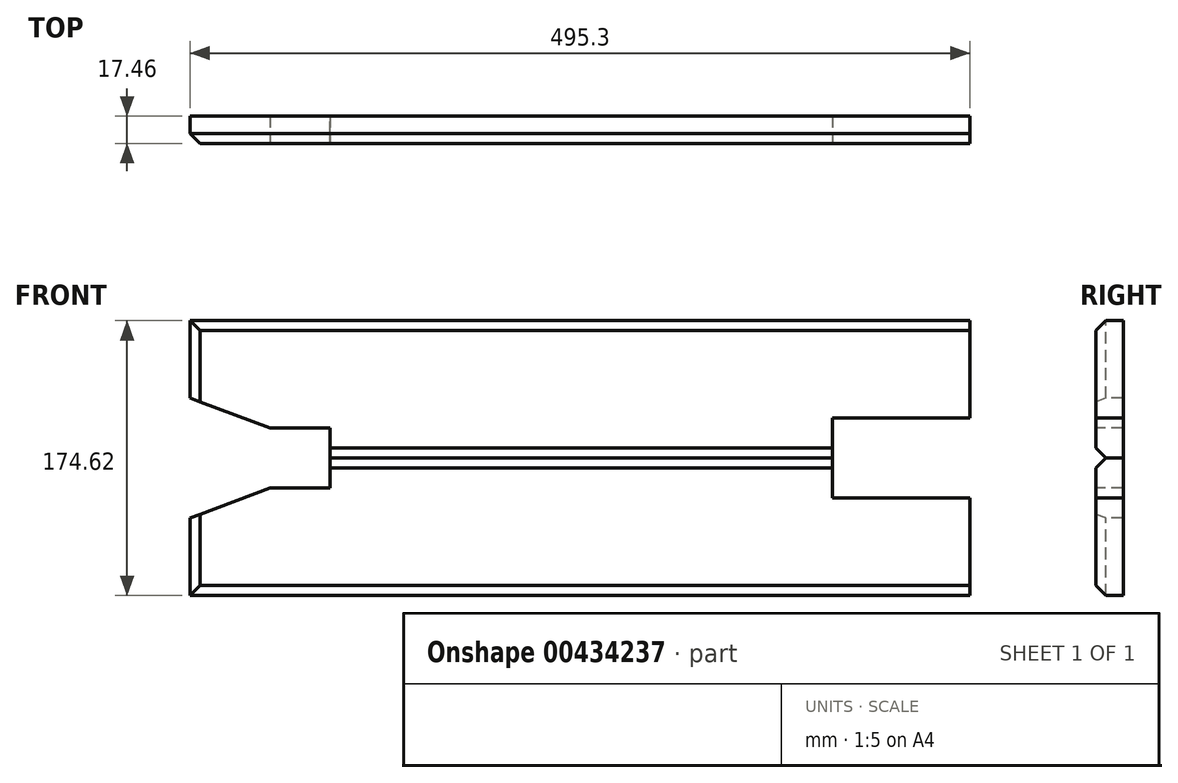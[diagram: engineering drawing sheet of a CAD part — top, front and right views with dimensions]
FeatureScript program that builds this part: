
annotation { "Feature Type Name" : "Feature", "Feature Type Description" : "" }
export const myFeature = defineFeature(function(context is Context, id is Id, definition is map)
    precondition{}
    {
        {
            var Q0;
            Q0=qCreatedBy(makeId("Front.planeOp"),FACE);
            var sketch = newSketch(context, id + "F0", { "sketchPlane" : qUnion([Q0])});
            skLineSegment(sketch, "E0.bottom", {"start": v(0, 0) * mm, "end": v(495.3, 0) * mm});
            skLineSegment(sketch, "E0.top", {"start": v(0, 87.31) * mm, "end": v(495.3, 87.31) * mm});
            skLineSegment(sketch, "E0.left", {"start": v(0, 0) * mm, "end": v(0, 87.31) * mm});
            skLineSegment(sketch, "E0.right", {"start": v(495.3, 0) * mm, "end": v(495.3, 87.31) * mm});
            skSolve(sketch);
        }
        {
            var Q0;
            Q0 = qSketchRegion(id + "F0", true);
            extrude(context, id + "F1", {"entities" : qUnion([Q0]), "depth" : 17.46 * mm});
        }
        {
            var Q0;
            Q0=makeQuery(id+"F1.opExtrude","SWEPT_FACE",FACE,{"disambiguationData":[OSD([sQuery(id+"F0.wireOp",EDGE,"E0.bottom")])]});
            var sketch = newSketch(context, id + "F2", { "sketchPlane" : qUnion([Q0])});
            skLineSegment(sketch, "E1.bottom", {"start": v(0, 0) * mm, "end": v(495.3, 0) * mm});
            skLineSegment(sketch, "E1.top", {"start": v(0, 17.46) * mm, "end": v(495.3, 17.46) * mm});
            skLineSegment(sketch, "E1.left", {"start": v(0, 0) * mm, "end": v(0, 17.46) * mm});
            skLineSegment(sketch, "E1.right", {"start": v(495.3, 0) * mm, "end": v(495.3, 17.46) * mm});
            skSolve(sketch);
        }
        {
            var Q0;
            Q0 = qSketchRegion(id + "F2", true);
            extrude(context, id + "F3", {"entities" : qUnion([Q0]), "depth" : 87.31 * mm});
        }
        {
            var Q0;
            Q0=makeQuery(id+"F3.opExtrude","SWEPT_FACE",FACE,{"disambiguationData":[OSD([sQuery(id+"F2.wireOp",EDGE,"E1.top")])]});
            var sketch = newSketch(context, id + "F4", { "sketchPlane" : qUnion([Q0])});
            skLineSegment(sketch, "E2", {"start": v(495.3, 0) * mm, "end": v(495.3, -25.4) * mm});
            skLineSegment(sketch, "E3", {"start": v(495.3, -25.4) * mm, "end": v(407.99, -25.4) * mm});
            skLineSegment(sketch, "E4", {"start": v(407.99, -25.4) * mm, "end": v(407.99, 0) * mm});
            skLineSegment(sketch, "E5", {"start": v(407.99, 0) * mm, "end": v(407.99, 25.4) * mm});
            skLineSegment(sketch, "E6", {"start": v(407.99, 25.4) * mm, "end": v(495.3, 25.4) * mm});
            skLineSegment(sketch, "E7", {"start": v(495.3, 25.4) * mm, "end": v(495.3, 0) * mm});
            skLineSegment(sketch, "E8", {"start": v(0, 38.1) * mm, "end": v(50.8, 19.05) * mm});
            skLineSegment(sketch, "E9", {"start": v(50.8, -19.05) * mm, "end": v(0, -38.1) * mm});
            skLineSegment(sketch, "E10", {"start": v(0, -38.1) * mm, "end": v(0, 0) * mm});
            skLineSegment(sketch, "E11", {"start": v(0, 0) * mm, "end": v(0, 38.1) * mm});
            skLineSegment(sketch, "E12", {"start": v(50.8, 19.05) * mm, "end": v(88.9, 19.05) * mm});
            skLineSegment(sketch, "E13", {"start": v(88.9, 19.05) * mm, "end": v(88.9, 0) * mm});
            skLineSegment(sketch, "E14", {"start": v(88.9, 0) * mm, "end": v(88.9, -19.05) * mm});
            skLineSegment(sketch, "E15", {"start": v(88.9, -19.05) * mm, "end": v(50.8, -19.05) * mm});
            skLineSegment(sketch, "E16", {"start": v(0, 0) * mm, "end": v(88.9, 0) * mm});
            skSolve(sketch);
        }
        {
            var Q0;
            Q0 = qSketchRegion(id + "F4", true);
            extrude(context, id + "F5", {"entities" : qUnion([Q0]), "operationType" : NewBodyOperationType.REMOVE, "oppositeDirection" : true, "depth" : 25.4 * mm});
        }
        {
            var Q0;
            Q0=makeQuery(id+"F1.opExtrude","CAP_EDGE",EDGE,{"disambiguationData":[OSD([sQuery(id+"F0.wireOp",EDGE,"E0.top")])],"isStart":false});
            var Q1;
            Q1=makeQuery(id+"F3.opExtrude","CAP_EDGE",EDGE,{"disambiguationData":[OSD([sQuery(id+"F2.wireOp",EDGE,"E1.top")])],"isStart":false});
            var Q2;
            Q2=makeQuery(id+"F3.opExtrude","CAP_EDGE",EDGE,{"disambiguationData":[OSD([sQuery(id+"F2.wireOp",EDGE,"E1.top")])],"isStart":true});
            var Q3;
            Q3=makeQuery(id+"F1.opExtrude","CAP_EDGE",EDGE,{"disambiguationData":[OSD([sQuery(id+"F0.wireOp",EDGE,"E0.left")])],"isStart":false});
            var Q4;
            Q4=makeQuery(id+"F3.opExtrude","SWEPT_EDGE",EDGE,{"disambiguationData":[OSD([sQuery(id+"F2.wireOp",EDGE,"E1.top"),sQuery(id+"F2.wireOp",EDGE,"E1.left")])]});
            chamfer(context, id + "F6", {"entities" : qUnion([Q0, Q1, Q2, Q3, Q4]), "width" : 6.35 * mm, "tangentPropagation" : true});
        }
        {
            var Q0;
            Q0=makeQuery(id+"F1.opExtrude","CAP_EDGE",EDGE,{"disambiguationData":[OSD([sQuery(id+"F0.wireOp",EDGE,"E0.bottom")])],"isStart":false});
            chamfer(context, id + "F7", {"entities" : qUnion([Q0]), "width" : 6.35 * mm, "tangentPropagation" : true});
        }
    });
